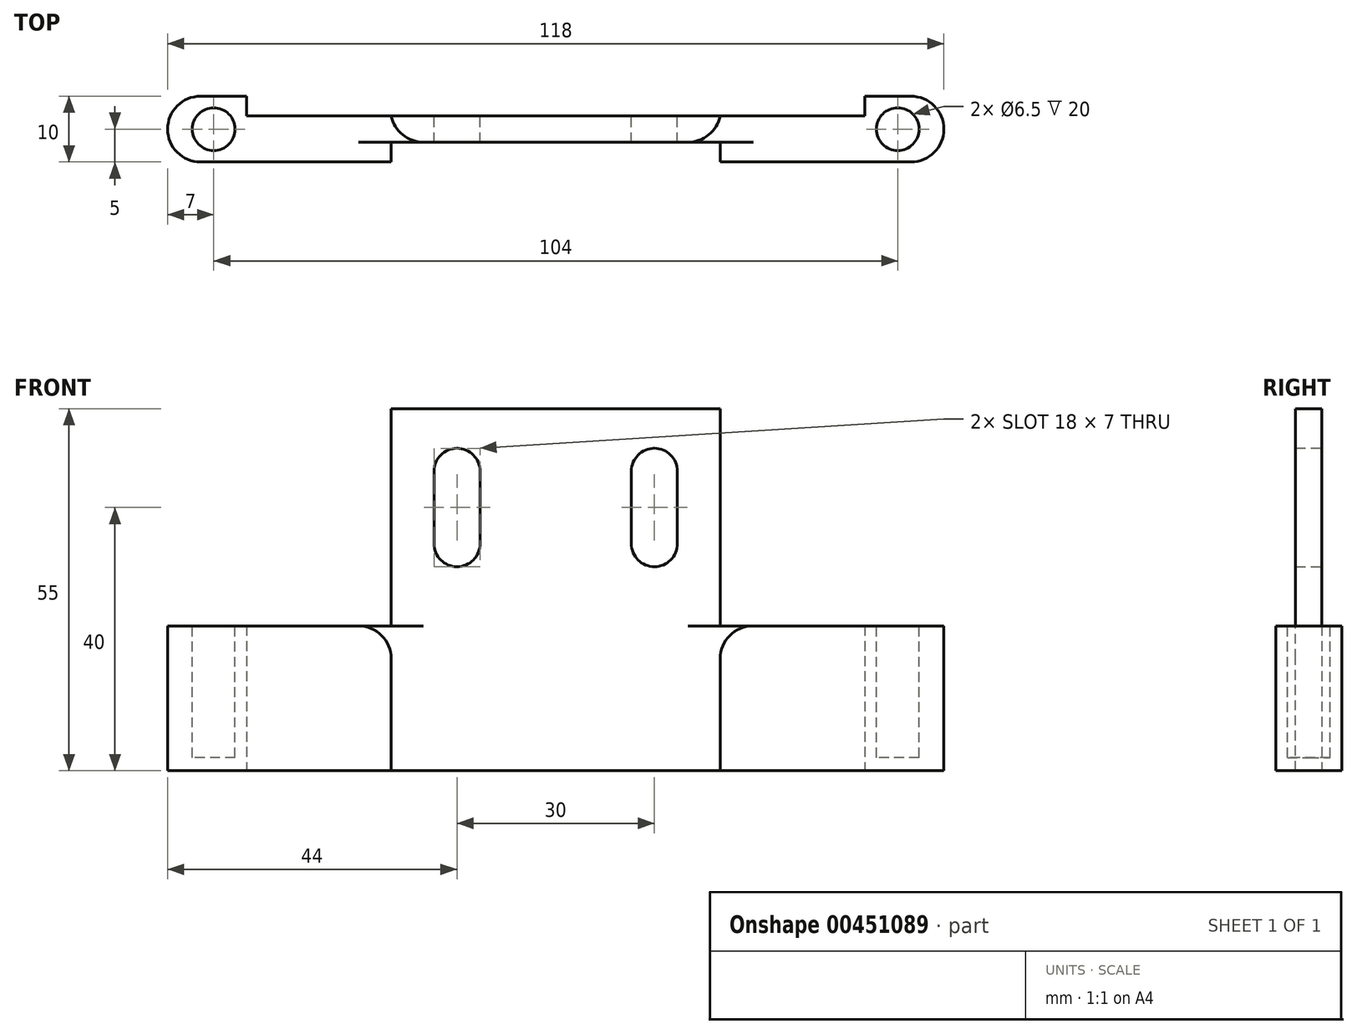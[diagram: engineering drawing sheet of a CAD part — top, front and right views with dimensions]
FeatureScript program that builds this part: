
annotation { "Feature Type Name" : "Feature", "Feature Type Description" : "" }
export const myFeature = defineFeature(function(context is Context, id is Id, definition is map)
    precondition{}
    {
        {
            var Q0;
            Q0=qCreatedBy(makeId("Front.planeOp"),FACE);
            var sketch = newSketch(context, id + "F0", { "sketchPlane" : qUnion([Q0])});
            skLineSegment(sketch, "E0.bottom", {"start": v(25, 0) * mm, "end": v(-25, 0) * mm});
            skLineSegment(sketch, "E0.top", {"start": v(25, 55) * mm, "end": v(-25, 55) * mm});
            skLineSegment(sketch, "E0.left", {"start": v(25, 0) * mm, "end": v(25, 55) * mm});
            skLineSegment(sketch, "E0.right", {"start": v(-25, 0) * mm, "end": v(-25, 55) * mm});
            skPoint(sketch, "E0.middle", {"position": v(0, 27.5) * mm});
            skLineSegment(sketch, "E1.bottom", {"start": v(-11.5, 34.5) * mm, "end": v(-18.5, 34.5) * mm, "construction": true});
            skLineSegment(sketch, "E1.top", {"start": v(-11.5, 45.5) * mm, "end": v(-18.5, 45.5) * mm, "construction": true});
            skLineSegment(sketch, "E1.left", {"start": v(-11.5, 34.5) * mm, "end": v(-11.5, 45.5) * mm});
            skLineSegment(sketch, "E1.right", {"start": v(-18.5, 34.5) * mm, "end": v(-18.5, 45.5) * mm});
            skPoint(sketch, "E1.middle", {"position": v(-15, 40) * mm});
            skArc(sketch, "E2", {"start": v(-11.5, 45.5) * mm, "mid": v(-15, 49) * mm, "end": v(-18.5, 45.5) * mm});
            skArc(sketch, "E3", {"start": v(-18.5, 34.5) * mm, "mid": v(-15, 31) * mm, "end": v(-11.5, 34.5) * mm});
            skLineSegment(sketch, "E4.MirrorCS", {"start": v(11.5, 34.5) * mm, "end": v(18.5, 34.5) * mm, "construction": true});
            skLineSegment(sketch, "E5.MirrorCS", {"start": v(11.5, 45.5) * mm, "end": v(18.5, 45.5) * mm, "construction": true});
            skPoint(sketch, "E6.MirrorP", {"position": v(15, 40) * mm});
            skArc(sketch, "E7.MirrorCS", {"start": v(11.5, 45.5) * mm, "mid": v(15, 49) * mm, "end": v(18.5, 45.5) * mm});
            skLineSegment(sketch, "E8.MirrorCS", {"start": v(11.5, 34.5) * mm, "end": v(11.5, 45.5) * mm});
            skLineSegment(sketch, "E9.MirrorCS", {"start": v(18.5, 34.5) * mm, "end": v(18.5, 45.5) * mm});
            skArc(sketch, "E10.MirrorCS", {"start": v(18.5, 34.5) * mm, "mid": v(15, 31) * mm, "end": v(11.5, 34.5) * mm});
            skSolve(sketch);
        }
        {
            var Q0;
            Q0 = qSketchRegion(id + "F0", true);
            extrude(context, id + "F1", {"entities" : qUnion([Q0]), "depth" : 4 * mm, "offsetDistance" : 25 * mm});
        }
        {
            var Q0;
            Q0=makeQuery(id+"F1.opExtrude","CAP_FACE",FACE,{"disambiguationData":[OSD([sQuery(id+"F0.wireOp",EDGE,"E0.bottom"),sQuery(id+"F0.wireOp",EDGE,"E0.top"),sQuery(id+"F0.wireOp",EDGE,"E0.left"),sQuery(id+"F0.wireOp",EDGE,"E0.right"),sQuery(id+"F0.wireOp",EDGE,"E1.left"),sQuery(id+"F0.wireOp",EDGE,"E1.right"),sQuery(id+"F0.wireOp",EDGE,"E2"),sQuery(id+"F0.wireOp",EDGE,"E3"),sQuery(id+"F0.wireOp",EDGE,"E7.MirrorCS"),sQuery(id+"F0.wireOp",EDGE,"E8.MirrorCS"),sQuery(id+"F0.wireOp",EDGE,"E9.MirrorCS"),sQuery(id+"F0.wireOp",EDGE,"E10.MirrorCS")])],"isStart":true});
            var sketch = newSketch(context, id + "F2", { "sketchPlane" : qUnion([Q0])});
            skLineSegment(sketch, "E11.bottom", {"start": v(59, 0) * mm, "end": v(25, 0) * mm});
            skLineSegment(sketch, "E11.top", {"start": v(59, 22) * mm, "end": v(25, 22) * mm});
            skLineSegment(sketch, "E11.left", {"start": v(25, 0) * mm, "end": v(25, 22) * mm});
            skLineSegment(sketch, "E11.right", {"start": v(59, 0) * mm, "end": v(59, 22) * mm});
            skLineSegment(sketch, "E12.MirrorCS", {"start": v(-59, 22) * mm, "end": v(-25, 22) * mm});
            skLineSegment(sketch, "E13.MirrorCS", {"start": v(-59, 0) * mm, "end": v(-59, 22) * mm});
            skLineSegment(sketch, "E14.MirrorCS", {"start": v(-25, 0) * mm, "end": v(-25, 22) * mm});
            skLineSegment(sketch, "E15.MirrorCS", {"start": v(-59, 0) * mm, "end": v(-25, 0) * mm});
            skSolve(sketch);
        }
        {
            var Q0;
            Q0 = qSketchRegion(id + "F2", true);
            extrude(context, id + "F3", {"entities" : qUnion([Q0]), "operationType" : NewBodyOperationType.ADD, "oppositeDirection" : true, "depth" : 7 * mm, "offsetDistance" : 25 * mm});
        }
        {
            var Q0;
            Q0=makeQuery(id+"F3.boolean.opBoolean","MERGE",FACE,{"derivedFrom":[makeQuery(id+"F1.opExtrude","CAP_FACE",FACE,{"disambiguationData":[OSD([sQuery(id+"F0.wireOp",EDGE,"E0.bottom"),sQuery(id+"F0.wireOp",EDGE,"E0.top"),sQuery(id+"F0.wireOp",EDGE,"E0.left"),sQuery(id+"F0.wireOp",EDGE,"E0.right"),sQuery(id+"F0.wireOp",EDGE,"E1.left"),sQuery(id+"F0.wireOp",EDGE,"E1.right"),sQuery(id+"F0.wireOp",EDGE,"E2"),sQuery(id+"F0.wireOp",EDGE,"E3"),sQuery(id+"F0.wireOp",EDGE,"E7.MirrorCS"),sQuery(id+"F0.wireOp",EDGE,"E8.MirrorCS"),sQuery(id+"F0.wireOp",EDGE,"E9.MirrorCS"),sQuery(id+"F0.wireOp",EDGE,"E10.MirrorCS")])],"isStart":true}),makeQuery(id+"F3.opExtrude","CAP_FACE",FACE,{"disambiguationData":[OSD([sQuery(id+"F2.wireOp",EDGE,"E11.bottom"),sQuery(id+"F2.wireOp",EDGE,"E11.top"),sQuery(id+"F2.wireOp",EDGE,"E11.left"),sQuery(id+"F2.wireOp",EDGE,"E11.right")])],"isStart":true}),makeQuery(id+"F3.opExtrude","CAP_FACE",FACE,{"disambiguationData":[OSD([sQuery(id+"F2.wireOp",EDGE,"E12.MirrorCS"),sQuery(id+"F2.wireOp",EDGE,"E13.MirrorCS"),sQuery(id+"F2.wireOp",EDGE,"E14.MirrorCS"),sQuery(id+"F2.wireOp",EDGE,"E15.MirrorCS")])],"isStart":true})]});
            var sketch = newSketch(context, id + "F4", { "sketchPlane" : qUnion([Q0])});
            skLineSegment(sketch, "E16.bottom", {"start": v(59, 22) * mm, "end": v(47, 22) * mm});
            skLineSegment(sketch, "E16.top", {"start": v(59, 0) * mm, "end": v(47, 0) * mm});
            skLineSegment(sketch, "E16.left", {"start": v(59, 22) * mm, "end": v(59, 0) * mm});
            skLineSegment(sketch, "E16.right", {"start": v(47, 22) * mm, "end": v(47, 0) * mm});
            skLineSegment(sketch, "E17.MirrorCS", {"start": v(-47, 22) * mm, "end": v(-47, 0) * mm});
            skLineSegment(sketch, "E18.MirrorCS", {"start": v(-59, 22) * mm, "end": v(-59, 0) * mm});
            skLineSegment(sketch, "E19.MirrorCS", {"start": v(-59, 0) * mm, "end": v(-47, 0) * mm});
            skLineSegment(sketch, "E20.MirrorCS", {"start": v(-59, 22) * mm, "end": v(-47, 22) * mm});
            skSolve(sketch);
        }
        {
            var Q0;
            Q0 = qSketchRegion(id + "F4", true);
            extrude(context, id + "F5", {"entities" : qUnion([Q0]), "operationType" : NewBodyOperationType.ADD, "depth" : 3 * mm, "offsetDistance" : 25 * mm});
        }
        {
            var Q0;
            Q0=makeQuery(id+"F3.opExtrude","SWEPT_FACE",FACE,{"disambiguationData":[OSD([sQuery(id+"F2.wireOp",EDGE,"E11.top")])]});
            var sketch = newSketch(context, id + "F6", { "sketchPlane" : qUnion([Q0])});
            skCircle(sketch, "E21", {"center": v(-52, -2) * mm, "radius": 3.25 * mm});
            skCircle(sketch, "E22.MirrorC", {"center": v(52, -2) * mm, "radius": 3.25 * mm});
            skSolve(sketch);
        }
        {
            var Q0;
            Q0 = qSketchRegion(id + "F6", true);
            extrude(context, id + "F7", {"entities" : qUnion([Q0]), "operationType" : NewBodyOperationType.REMOVE, "oppositeDirection" : true, "depth" : 20 * mm, "offsetDistance" : 25 * mm});
        }
        {
            var Q0;
            Q0=makeQuery(id+"F5.opExtrude","CAP_EDGE",EDGE,{"disambiguationData":[OSD([sQuery(id+"F4.wireOp",EDGE,"E16.right")])],"isStart":true});
            var Q1;
            Q1=makeQuery(id+"F5.opExtrude","CAP_EDGE",EDGE,{"disambiguationData":[OSD([sQuery(id+"F4.wireOp",EDGE,"E17.MirrorCS")])],"isStart":true});
            var Q2;
            {var subQ0=sQuery(id+"F0.wireOp",EDGE,"E0.right");Q2=makeQuery(id+"F3.boolean.opBoolean","SPLIT",EDGE,{"disambiguationData":[topologyDisambiguationEdgeConnected([makeQuery(id+"F3.opExtrude","SWEPT_FACE",FACE,{"disambiguationData":[OSD([sQuery(id+"F2.wireOp",EDGE,"E11.left")])]})])],"derivedFrom":makeQuery(id+"F1.opExtrude","CAP_EDGE",EDGE,{"disambiguationData":[OSD([subQ0])],"isStart":false})});}
            var Q3;
            {var subQ0=sQuery(id+"F0.wireOp",EDGE,"E0.left");Q3=makeQuery(id+"F3.boolean.opBoolean","SPLIT",EDGE,{"disambiguationData":[topologyDisambiguationEdgeConnected([makeQuery(id+"F3.opExtrude","SWEPT_FACE",FACE,{"disambiguationData":[OSD([sQuery(id+"F2.wireOp",EDGE,"E14.MirrorCS")])]})])],"derivedFrom":makeQuery(id+"F1.opExtrude","CAP_EDGE",EDGE,{"disambiguationData":[OSD([subQ0])],"isStart":false})});}
            var Q4;
            Q4=makeQuery(id+"F5.opExtrude","CAP_EDGE",EDGE,{"disambiguationData":[OSD([sQuery(id+"F4.wireOp",EDGE,"E16.left")])],"isStart":false});
            var Q5;
            Q5=makeQuery(id+"F3.opExtrude","CAP_EDGE",EDGE,{"disambiguationData":[OSD([sQuery(id+"F2.wireOp",EDGE,"E11.right")])],"isStart":false});
            var Q6;
            Q6=makeQuery(id+"F3.opExtrude","CAP_EDGE",EDGE,{"disambiguationData":[OSD([sQuery(id+"F2.wireOp",EDGE,"E13.MirrorCS")])],"isStart":false});
            var Q7;
            Q7=makeQuery(id+"F5.opExtrude","CAP_EDGE",EDGE,{"disambiguationData":[OSD([sQuery(id+"F4.wireOp",EDGE,"E18.MirrorCS")])],"isStart":false});
            fillet(context, id + "F8", {"entities" : qUnion([Q0, Q1, Q2, Q3, Q4, Q5, Q6, Q7]), "tangentPropagation" : true, "radius" : 5 * mm, "defaultsChanged" : false, "vertexSettings" : [], "allowEdgeOverflow" : false});
        }
        {
            var Q0;
            {var subQ0=sQuery(id+"F0.wireOp",EDGE,"E0.right");var subQ1=sQuery(id+"F2.wireOp",EDGE,"E11.top");Q0=makeQuery(id+"F3.boolean.opBoolean","SPLIT",EDGE,{"disambiguationData":[topologyDisambiguationEdgeConnected([makeQuery(id+"F1.opExtrude","SWEPT_FACE",FACE,{"disambiguationData":[OSD([subQ0])]})])],"derivedFrom":makeQuery(id+"F3.opExtrude","SWEPT_EDGE",EDGE,{"disambiguationData":[OSD([subQ0,subQ1,sQuery(id+"F2.wireOp",EDGE,"E11.left")])]})});}
            var Q1;
            {var subQ0=sQuery(id+"F0.wireOp",EDGE,"E0.right");Q1=makeQuery(id+"F8.opFillet","TWEAK_EDGE",EDGE,{"derivedFrom":[makeQuery(id+"F3.boolean.opBoolean","TWEAK_VERTEX",VERTEX,{"derivedFrom":[makeQuery(id+"F1.opExtrude","CAP_FACE",FACE,{"disambiguationData":[OSD([sQuery(id+"F0.wireOp",EDGE,"E0.bottom"),sQuery(id+"F0.wireOp",EDGE,"E0.top"),sQuery(id+"F0.wireOp",EDGE,"E0.left"),subQ0,sQuery(id+"F0.wireOp",EDGE,"E1.left"),sQuery(id+"F0.wireOp",EDGE,"E1.right"),sQuery(id+"F0.wireOp",EDGE,"E2"),sQuery(id+"F0.wireOp",EDGE,"E3"),sQuery(id+"F0.wireOp",EDGE,"E7.MirrorCS"),sQuery(id+"F0.wireOp",EDGE,"E8.MirrorCS"),sQuery(id+"F0.wireOp",EDGE,"E9.MirrorCS"),sQuery(id+"F0.wireOp",EDGE,"E10.MirrorCS")])],"isStart":false}),makeQuery(id+"F1.opExtrude","SWEPT_FACE",FACE,{"disambiguationData":[OSD([subQ0])]}),makeQuery(id+"F3.opExtrude","SWEPT_FACE",FACE,{"disambiguationData":[OSD([sQuery(id+"F2.wireOp",EDGE,"E11.top")])]}),makeQuery(id+"F3.opExtrude","SWEPT_FACE",FACE,{"disambiguationData":[OSD([sQuery(id+"F2.wireOp",EDGE,"E11.left")])]})]})]});}
            var Q2;
            {var subQ0=sQuery(id+"F0.wireOp",EDGE,"E0.left");Q2=makeQuery(id+"F8.opFillet","TWEAK_EDGE",EDGE,{"derivedFrom":[makeQuery(id+"F3.boolean.opBoolean","TWEAK_VERTEX",VERTEX,{"derivedFrom":[makeQuery(id+"F1.opExtrude","CAP_FACE",FACE,{"disambiguationData":[OSD([sQuery(id+"F0.wireOp",EDGE,"E0.bottom"),sQuery(id+"F0.wireOp",EDGE,"E0.top"),subQ0,sQuery(id+"F0.wireOp",EDGE,"E0.right"),sQuery(id+"F0.wireOp",EDGE,"E1.left"),sQuery(id+"F0.wireOp",EDGE,"E1.right"),sQuery(id+"F0.wireOp",EDGE,"E2"),sQuery(id+"F0.wireOp",EDGE,"E3"),sQuery(id+"F0.wireOp",EDGE,"E7.MirrorCS"),sQuery(id+"F0.wireOp",EDGE,"E8.MirrorCS"),sQuery(id+"F0.wireOp",EDGE,"E9.MirrorCS"),sQuery(id+"F0.wireOp",EDGE,"E10.MirrorCS")])],"isStart":false}),makeQuery(id+"F1.opExtrude","SWEPT_FACE",FACE,{"disambiguationData":[OSD([subQ0])]}),makeQuery(id+"F3.opExtrude","SWEPT_FACE",FACE,{"disambiguationData":[OSD([sQuery(id+"F2.wireOp",EDGE,"E12.MirrorCS")])]}),makeQuery(id+"F3.opExtrude","SWEPT_FACE",FACE,{"disambiguationData":[OSD([sQuery(id+"F2.wireOp",EDGE,"E14.MirrorCS")])]})]})]});}
            var Q3;
            {var subQ0=sQuery(id+"F0.wireOp",EDGE,"E0.left");var subQ1=sQuery(id+"F2.wireOp",EDGE,"E12.MirrorCS");Q3=makeQuery(id+"F3.boolean.opBoolean","SPLIT",EDGE,{"disambiguationData":[topologyDisambiguationEdgeConnected([makeQuery(id+"F1.opExtrude","SWEPT_FACE",FACE,{"disambiguationData":[OSD([subQ0])]})])],"derivedFrom":makeQuery(id+"F3.opExtrude","SWEPT_EDGE",EDGE,{"disambiguationData":[OSD([subQ0,subQ1,sQuery(id+"F2.wireOp",EDGE,"E14.MirrorCS")])]})});}
            fillet(context, id + "F9", {"entities" : qUnion([Q0, Q1, Q2, Q3]), "tangentPropagation" : true, "radius" : 5 * mm, "defaultsChanged" : false, "vertexSettings" : [], "allowEdgeOverflow" : false});
        }
    });
